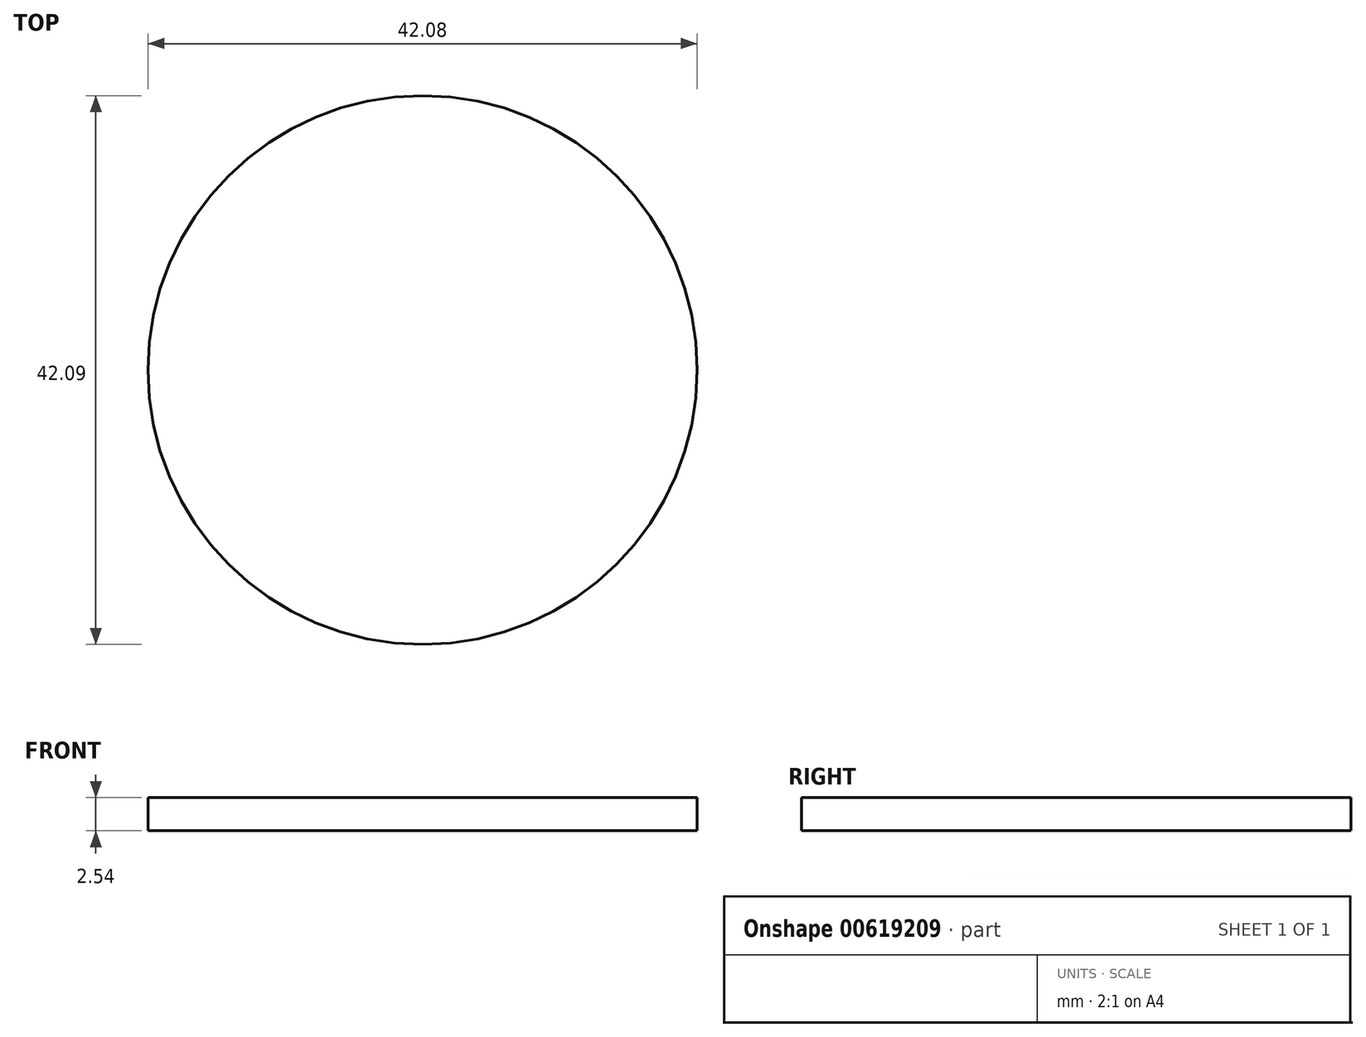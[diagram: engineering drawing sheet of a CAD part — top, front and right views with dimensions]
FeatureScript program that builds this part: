
annotation { "Feature Type Name" : "Feature", "Feature Type Description" : "" }
export const myFeature = defineFeature(function(context is Context, id is Id, definition is map)
    precondition{}
    {
        {
            var Q0;
            Q0=qCreatedBy(makeId("Top.planeOp"),FACE);
            var sketch = newSketch(context, id + "F0", { "sketchPlane" : qUnion([Q0])});
            skCircle(sketch, "E0", {"center": v(39.73, 6.2) * mm, "radius": 21.04 * mm});
            skSolve(sketch);
        }
        {
            var Q0;
            Q0=makeQuery(id+"F0.imprint","IMPRINT",FACE,{"disambiguationData":[TD([[makeQuery(id+"F0.imprint","IMPRINT",EDGE,{"derivedFrom":sQuery(id+"F0.wireOp",EDGE,"E0")}),1.0]])]});
            extrude(context, id + "F1", {"entities" : qUnion([Q0]), "depth" : 2.54 * mm, "offsetDistance" : 25.4 * mm});
        }
    });
